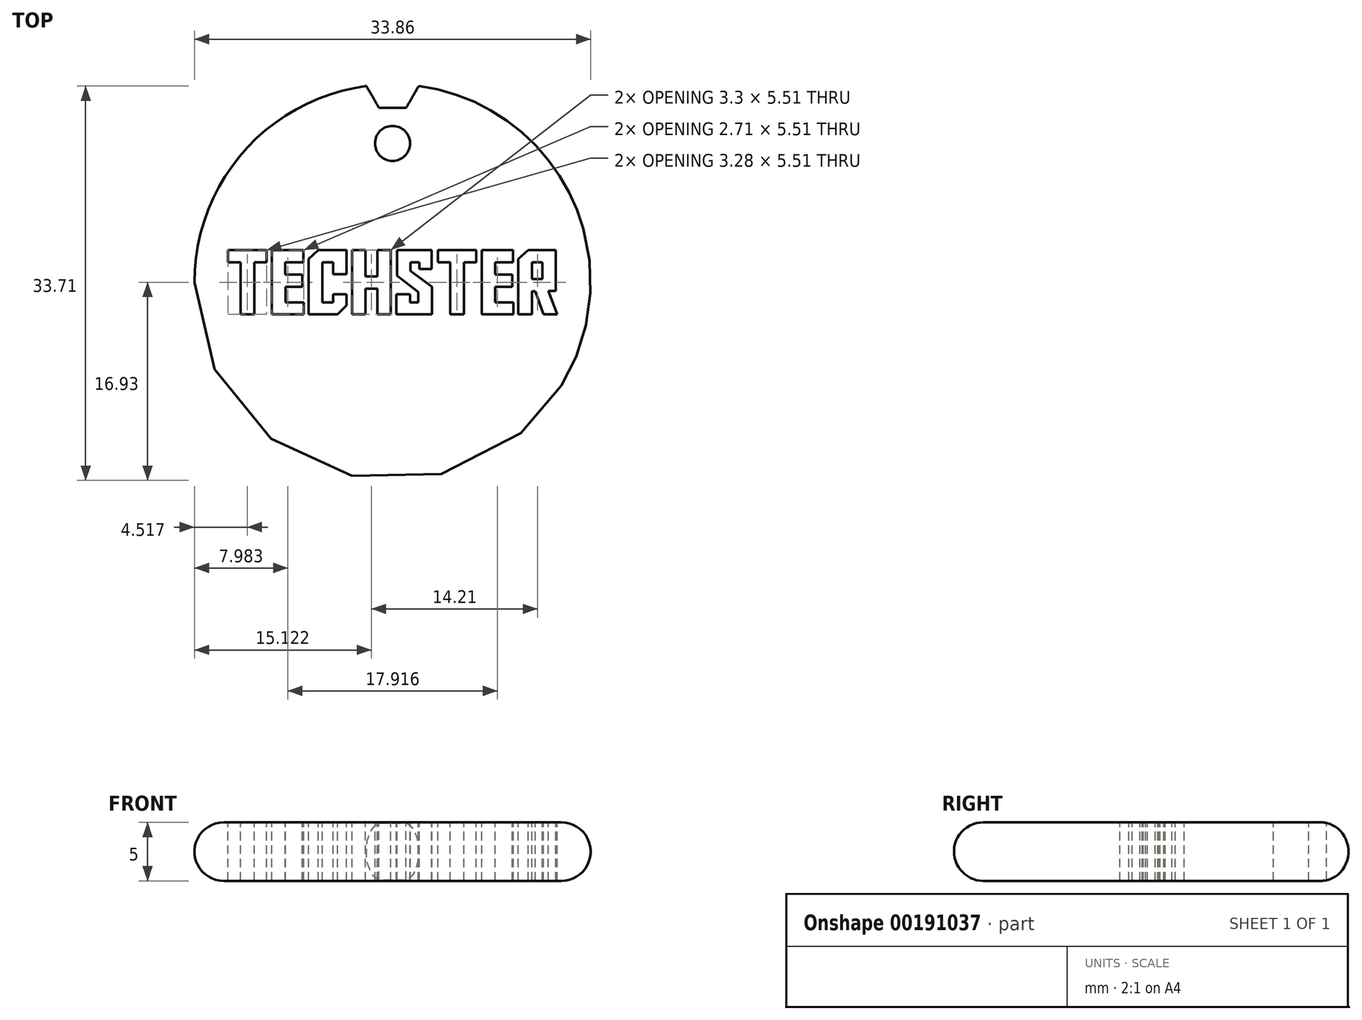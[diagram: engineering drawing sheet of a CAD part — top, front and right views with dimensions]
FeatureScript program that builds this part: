
annotation { "Feature Type Name" : "Feature", "Feature Type Description" : "" }
export const myFeature = defineFeature(function(context is Context, id is Id, definition is map)
    precondition{}
    {
        {
            var Q0;
            Q0=qCreatedBy(makeId("Front.planeOp"),FACE);
            var sketch = newSketch(context, id + "F0", { "sketchPlane" : qUnion([Q0])});
            skLineSegment(sketch, "E0.bottom", {"start": v(0, 0) * mm, "end": v(-14.43, 0) * mm});
            skLineSegment(sketch, "E0.top", {"start": v(0, 5) * mm, "end": v(-14.43, 5) * mm});
            skLineSegment(sketch, "E0.left", {"start": v(0, 0) * mm, "end": v(0, 5) * mm});
            skArc(sketch, "E1", {"start": v(-14.43, 5) * mm, "mid": v(-16.93, 2.5) * mm, "end": v(-14.43, 0) * mm});
            skSolve(sketch);
        }
        {
            var Q0;
            Q0 = qSketchRegion(id + "F0", true);
            var Q1;
            Q1=sQuery(id+"F0.wireOp",EDGE,"E0.left");
            revolve(context, id + "F1", {"entities" : qUnion([Q0]), "axis" : qUnion([Q1]), "revolveType" : RevolveType.FULL});
        }
        {
            var Q0;
            Q0=qCreatedBy(makeId("Top.planeOp"),FACE);
            cPlane(context, id + "F2", {"entities" : qUnion([Q0]), "cplaneType" : CPlaneType.OFFSET, "offset" : 6 * mm, "width" : 152.4 * mm, "height" : 152.4 * mm});
        }
        {
            var Q0;
            Q0=qCreatedBy(id+"F2.planeOp",FACE);
            var sketch = newSketch(context, id + "F3", { "sketchPlane" : qUnion([Q0])});
            skCircle(sketch, "E2.cCircle", {"center": v(0, 16.9) * mm, "radius": 2 * mm, "construction": true});
            skLineSegment(sketch, "E2.0", {"start": v(1.15, 14.9) * mm, "end": v(-1.15, 14.9) * mm});
            skLineSegment(sketch, "E2.1", {"start": v(-1.15, 14.9) * mm, "end": v(-2.3, 16.9) * mm});
            skLineSegment(sketch, "E2.2", {"start": v(-2.3, 16.9) * mm, "end": v(-1.15, 18.9) * mm});
            skLineSegment(sketch, "E2.3", {"start": v(-1.15, 18.9) * mm, "end": v(1.15, 18.9) * mm});
            skLineSegment(sketch, "E2.4", {"start": v(1.15, 18.9) * mm, "end": v(2.3, 16.9) * mm});
            skLineSegment(sketch, "E2.5", {"start": v(2.3, 16.9) * mm, "end": v(1.15, 14.9) * mm});
            skPoint(sketch, "E2.0.midPoint", {"position": v(0, 14.9) * mm});
            skSolve(sketch);
        }
        {
            var Q0;
            Q0 = qSketchRegion(id + "F3", true);
            extrude(context, id + "F4", {"entities" : qUnion([Q0]), "operationType" : NewBodyOperationType.REMOVE, "oppositeDirection" : true, "depth" : 25.4 * mm});
        }
        {
            var Q0;
            Q0=qCreatedBy(id+"F2.planeOp",FACE);
            var sketch = newSketch(context, id + "F5", { "sketchPlane" : qUnion([Q0])});
            skCircle(sketch, "E3", {"center": v(0, 11.87) * mm, "radius": 1.5 * mm});
            skSolve(sketch);
        }
        {
            var Q0;
            Q0=makeQuery(id+"F5.imprint","IMPRINT",FACE,{"disambiguationData":[TD([[makeQuery(id+"F5.imprint","IMPRINT",EDGE,{"derivedFrom":sQuery(id+"F5.wireOp",EDGE,"E3")}),1.0]])]});
            extrude(context, id + "F6", {"entities" : qUnion([Q0]), "operationType" : NewBodyOperationType.REMOVE, "oppositeDirection" : true, "depth" : 25.4 * mm});
        }
        {
            var Q0;
            Q0=qCreatedBy(id+"F2.planeOp",FACE);
            var sketch = newSketch(context, id + "F7", { "sketchPlane" : qUnion([Q0])});
            skLineSegment(sketch, "E4", {"start": v(-10.77, 1.7) * mm, "end": v(-11.81, 1.7) * mm});
            skLineSegment(sketch, "E5", {"start": v(-11.81, 1.7) * mm, "end": v(-11.81, -2.76) * mm});
            skLineSegment(sketch, "E6", {"start": v(-11.81, -2.76) * mm, "end": v(-12.97, -2.76) * mm});
            skLineSegment(sketch, "E7", {"start": v(-12.97, -2.76) * mm, "end": v(-12.97, 1.7) * mm});
            skLineSegment(sketch, "E8", {"start": v(-12.97, 1.7) * mm, "end": v(-14.05, 1.7) * mm});
            skLineSegment(sketch, "E9", {"start": v(-14.05, 1.7) * mm, "end": v(-14.05, 2.76) * mm});
            skLineSegment(sketch, "E10", {"start": v(-14.05, 2.76) * mm, "end": v(-10.77, 2.76) * mm});
            skLineSegment(sketch, "E11", {"start": v(-10.77, 2.76) * mm, "end": v(-10.77, 1.7) * mm});
            skLineSegment(sketch, "E12", {"start": v(-10.3, 2.76) * mm, "end": v(-7.63, 2.76) * mm});
            skLineSegment(sketch, "E13", {"start": v(-7.63, 2.76) * mm, "end": v(-7.63, 1.7) * mm});
            skLineSegment(sketch, "E14", {"start": v(-7.63, 1.7) * mm, "end": v(-9.16, 1.7) * mm});
            skLineSegment(sketch, "E15", {"start": v(-9.16, 1.7) * mm, "end": v(-9.16, 0.64) * mm});
            skLineSegment(sketch, "E16", {"start": v(-9.16, 0.64) * mm, "end": v(-7.7, 0.64) * mm});
            skLineSegment(sketch, "E17", {"start": v(-7.7, 0.64) * mm, "end": v(-7.7, -0.38) * mm});
            skLineSegment(sketch, "E18", {"start": v(-7.7, -0.38) * mm, "end": v(-9.14, -0.38) * mm});
            skLineSegment(sketch, "E19", {"start": v(-9.14, -0.38) * mm, "end": v(-9.14, -1.71) * mm});
            skLineSegment(sketch, "E20", {"start": v(-9.14, -1.71) * mm, "end": v(-7.59, -1.71) * mm});
            skLineSegment(sketch, "E21", {"start": v(-7.59, -1.71) * mm, "end": v(-7.59, -2.76) * mm});
            skLineSegment(sketch, "E22", {"start": v(-7.59, -2.76) * mm, "end": v(-10.3, -2.76) * mm});
            skLineSegment(sketch, "E23", {"start": v(-10.3, -2.76) * mm, "end": v(-10.3, 2.76) * mm});
            skLineSegment(sketch, "E24", {"start": v(-5.08, -1.71) * mm, "end": v(-5.08, -1.04) * mm});
            skLineSegment(sketch, "E25", {"start": v(-5.08, -1.04) * mm, "end": v(-3.92, -1.04) * mm});
            skLineSegment(sketch, "E26", {"start": v(-3.92, -1.04) * mm, "end": v(-3.92, -2) * mm});
            skLineSegment(sketch, "E27", {"start": v(-3.92, -2) * mm, "end": v(-4.68, -2.76) * mm});
            skLineSegment(sketch, "E28", {"start": v(-4.68, -2.76) * mm, "end": v(-7.17, -2.76) * mm});
            skLineSegment(sketch, "E29", {"start": v(-7.17, -2.76) * mm, "end": v(-7.17, 2) * mm});
            skLineSegment(sketch, "E30", {"start": v(-7.17, 2) * mm, "end": v(-6.34, 2.76) * mm});
            skLineSegment(sketch, "E31", {"start": v(-6.34, 2.76) * mm, "end": v(-3.92, 2.76) * mm});
            skLineSegment(sketch, "E32", {"start": v(-3.92, 2.76) * mm, "end": v(-3.92, 0.67) * mm});
            skLineSegment(sketch, "E33", {"start": v(-3.92, 0.67) * mm, "end": v(-5.08, 0.67) * mm});
            skLineSegment(sketch, "E34", {"start": v(-5.08, 0.67) * mm, "end": v(-5.08, 1.7) * mm});
            skLineSegment(sketch, "E35", {"start": v(-5.08, 1.7) * mm, "end": v(-6, 1.7) * mm});
            skLineSegment(sketch, "E36", {"start": v(-6, 1.7) * mm, "end": v(-6, -1.71) * mm});
            skLineSegment(sketch, "E37", {"start": v(-6, -1.71) * mm, "end": v(-5.08, -1.71) * mm});
            skLineSegment(sketch, "E38", {"start": v(-2.3, 0.5) * mm, "end": v(-1.31, 0.5) * mm});
            skLineSegment(sketch, "E39", {"start": v(-1.31, 0.5) * mm, "end": v(-1.31, 2.76) * mm});
            skLineSegment(sketch, "E40", {"start": v(-1.31, 2.76) * mm, "end": v(-0.16, 2.76) * mm});
            skLineSegment(sketch, "E41", {"start": v(-0.16, 2.76) * mm, "end": v(-0.16, -2.76) * mm});
            skLineSegment(sketch, "E42", {"start": v(-0.16, -2.76) * mm, "end": v(-1.31, -2.76) * mm});
            skLineSegment(sketch, "E43", {"start": v(-1.31, -2.76) * mm, "end": v(-1.31, -0.55) * mm});
            skLineSegment(sketch, "E44", {"start": v(-1.31, -0.55) * mm, "end": v(-2.3, -0.55) * mm});
            skLineSegment(sketch, "E45", {"start": v(-2.3, -0.55) * mm, "end": v(-2.3, -2.76) * mm});
            skLineSegment(sketch, "E46", {"start": v(-2.3, -2.76) * mm, "end": v(-3.46, -2.76) * mm});
            skLineSegment(sketch, "E47", {"start": v(-3.46, -2.76) * mm, "end": v(-3.46, 2.76) * mm});
            skLineSegment(sketch, "E48", {"start": v(-3.46, 2.76) * mm, "end": v(-2.3, 2.76) * mm});
            skLineSegment(sketch, "E49", {"start": v(-2.3, 2.76) * mm, "end": v(-2.3, 0.5) * mm});
            skLineSegment(sketch, "E50", {"start": v(3.36, -2.76) * mm, "end": v(0.33, -2.76) * mm});
            skLineSegment(sketch, "E51", {"start": v(0.33, -2.76) * mm, "end": v(0.33, -1.04) * mm});
            skLineSegment(sketch, "E52", {"start": v(0.33, -1.04) * mm, "end": v(1.49, -1.04) * mm});
            skLineSegment(sketch, "E53", {"start": v(1.49, -1.04) * mm, "end": v(1.49, -1.71) * mm});
            skLineSegment(sketch, "E54", {"start": v(1.49, -1.71) * mm, "end": v(2.2, -1.71) * mm});
            skLineSegment(sketch, "E55", {"start": v(2.2, -1.71) * mm, "end": v(2.2, -0.83) * mm});
            skLineSegment(sketch, "E56", {"start": v(2.2, -0.83) * mm, "end": v(0.37, 0.55) * mm});
            skLineSegment(sketch, "E57", {"start": v(0.37, 0.55) * mm, "end": v(0.37, 2.76) * mm});
            skLineSegment(sketch, "E58", {"start": v(0.37, 2.76) * mm, "end": v(3.33, 2.76) * mm});
            skLineSegment(sketch, "E59", {"start": v(3.33, 2.76) * mm, "end": v(3.33, 1.12) * mm});
            skLineSegment(sketch, "E60", {"start": v(3.33, 1.12) * mm, "end": v(2.28, 1.12) * mm});
            skLineSegment(sketch, "E61", {"start": v(2.28, 1.12) * mm, "end": v(2.28, 1.7) * mm});
            skLineSegment(sketch, "E62", {"start": v(2.28, 1.7) * mm, "end": v(1.53, 1.7) * mm});
            skLineSegment(sketch, "E63", {"start": v(1.53, 1.7) * mm, "end": v(1.53, 0.98) * mm});
            skLineSegment(sketch, "E64", {"start": v(1.53, 0.98) * mm, "end": v(3.36, -0.4) * mm});
            skLineSegment(sketch, "E65", {"start": v(3.36, -0.4) * mm, "end": v(3.36, -2.76) * mm});
            skLineSegment(sketch, "E66", {"start": v(7.14, 1.7) * mm, "end": v(6.1, 1.7) * mm});
            skLineSegment(sketch, "E67", {"start": v(6.1, 1.7) * mm, "end": v(6.1, -2.76) * mm});
            skLineSegment(sketch, "E68", {"start": v(6.1, -2.76) * mm, "end": v(4.94, -2.76) * mm});
            skLineSegment(sketch, "E69", {"start": v(4.94, -2.76) * mm, "end": v(4.94, 1.7) * mm});
            skLineSegment(sketch, "E70", {"start": v(4.94, 1.7) * mm, "end": v(3.86, 1.7) * mm});
            skLineSegment(sketch, "E71", {"start": v(3.86, 1.7) * mm, "end": v(3.86, 2.76) * mm});
            skLineSegment(sketch, "E72", {"start": v(3.86, 2.76) * mm, "end": v(7.14, 2.76) * mm});
            skLineSegment(sketch, "E73", {"start": v(7.14, 2.76) * mm, "end": v(7.14, 1.7) * mm});
            skLineSegment(sketch, "E74", {"start": v(7.61, 2.76) * mm, "end": v(10.29, 2.76) * mm});
            skLineSegment(sketch, "E75", {"start": v(10.29, 2.76) * mm, "end": v(10.29, 1.7) * mm});
            skLineSegment(sketch, "E76", {"start": v(10.29, 1.7) * mm, "end": v(8.76, 1.7) * mm});
            skLineSegment(sketch, "E77", {"start": v(8.76, 1.7) * mm, "end": v(8.76, 0.64) * mm});
            skLineSegment(sketch, "E78", {"start": v(8.76, 0.64) * mm, "end": v(10.21, 0.64) * mm});
            skLineSegment(sketch, "E79", {"start": v(10.21, 0.64) * mm, "end": v(10.21, -0.38) * mm});
            skLineSegment(sketch, "E80", {"start": v(10.21, -0.38) * mm, "end": v(8.77, -0.38) * mm});
            skLineSegment(sketch, "E81", {"start": v(8.77, -0.38) * mm, "end": v(8.77, -1.71) * mm});
            skLineSegment(sketch, "E82", {"start": v(8.77, -1.71) * mm, "end": v(10.33, -1.71) * mm});
            skLineSegment(sketch, "E83", {"start": v(10.33, -1.71) * mm, "end": v(10.33, -2.76) * mm});
            skLineSegment(sketch, "E84", {"start": v(10.33, -2.76) * mm, "end": v(7.61, -2.76) * mm});
            skLineSegment(sketch, "E85", {"start": v(7.61, -2.76) * mm, "end": v(7.61, 2.76) * mm});
            skLineSegment(sketch, "E86", {"start": v(12.9, -2.76) * mm, "end": v(12.2, -0.76) * mm});
            skLineSegment(sketch, "E87", {"start": v(12.2, -0.76) * mm, "end": v(11.9, -0.76) * mm});
            skLineSegment(sketch, "E88", {"start": v(11.9, -0.76) * mm, "end": v(11.9, -2.76) * mm});
            skLineSegment(sketch, "E89", {"start": v(11.9, -2.76) * mm, "end": v(10.75, -2.76) * mm});
            skLineSegment(sketch, "E90", {"start": v(10.75, -2.76) * mm, "end": v(10.75, 1.98) * mm});
            skLineSegment(sketch, "E91", {"start": v(10.75, 1.98) * mm, "end": v(11.59, 2.76) * mm});
            skLineSegment(sketch, "E92", {"start": v(11.59, 2.76) * mm, "end": v(13.95, 2.76) * mm});
            skLineSegment(sketch, "E93", {"start": v(13.95, 2.76) * mm, "end": v(13.95, -0.75) * mm});
            skLineSegment(sketch, "E94", {"start": v(13.95, -0.75) * mm, "end": v(13.32, -0.75) * mm});
            skLineSegment(sketch, "E95", {"start": v(13.32, -0.75) * mm, "end": v(14.05, -2.76) * mm});
            skLineSegment(sketch, "E96", {"start": v(14.05, -2.76) * mm, "end": v(12.9, -2.76) * mm});
            skLineSegment(sketch, "E97", {"start": v(12.8, 0.27) * mm, "end": v(12.8, 1.7) * mm});
            skLineSegment(sketch, "E98", {"start": v(12.8, 1.7) * mm, "end": v(11.9, 1.7) * mm});
            skLineSegment(sketch, "E99", {"start": v(11.9, 1.7) * mm, "end": v(11.9, 0.27) * mm});
            skLineSegment(sketch, "E100", {"start": v(11.9, 0.27) * mm, "end": v(12.8, 0.27) * mm});
            skSolve(sketch);
        }
        {
            var Q0;
            Q0 = qSketchRegion(id + "F7", true);
            extrude(context, id + "F8", {"entities" : qUnion([Q0]), "operationType" : NewBodyOperationType.REMOVE, "oppositeDirection" : true, "depth" : 25.4 * mm});
        }
    });
